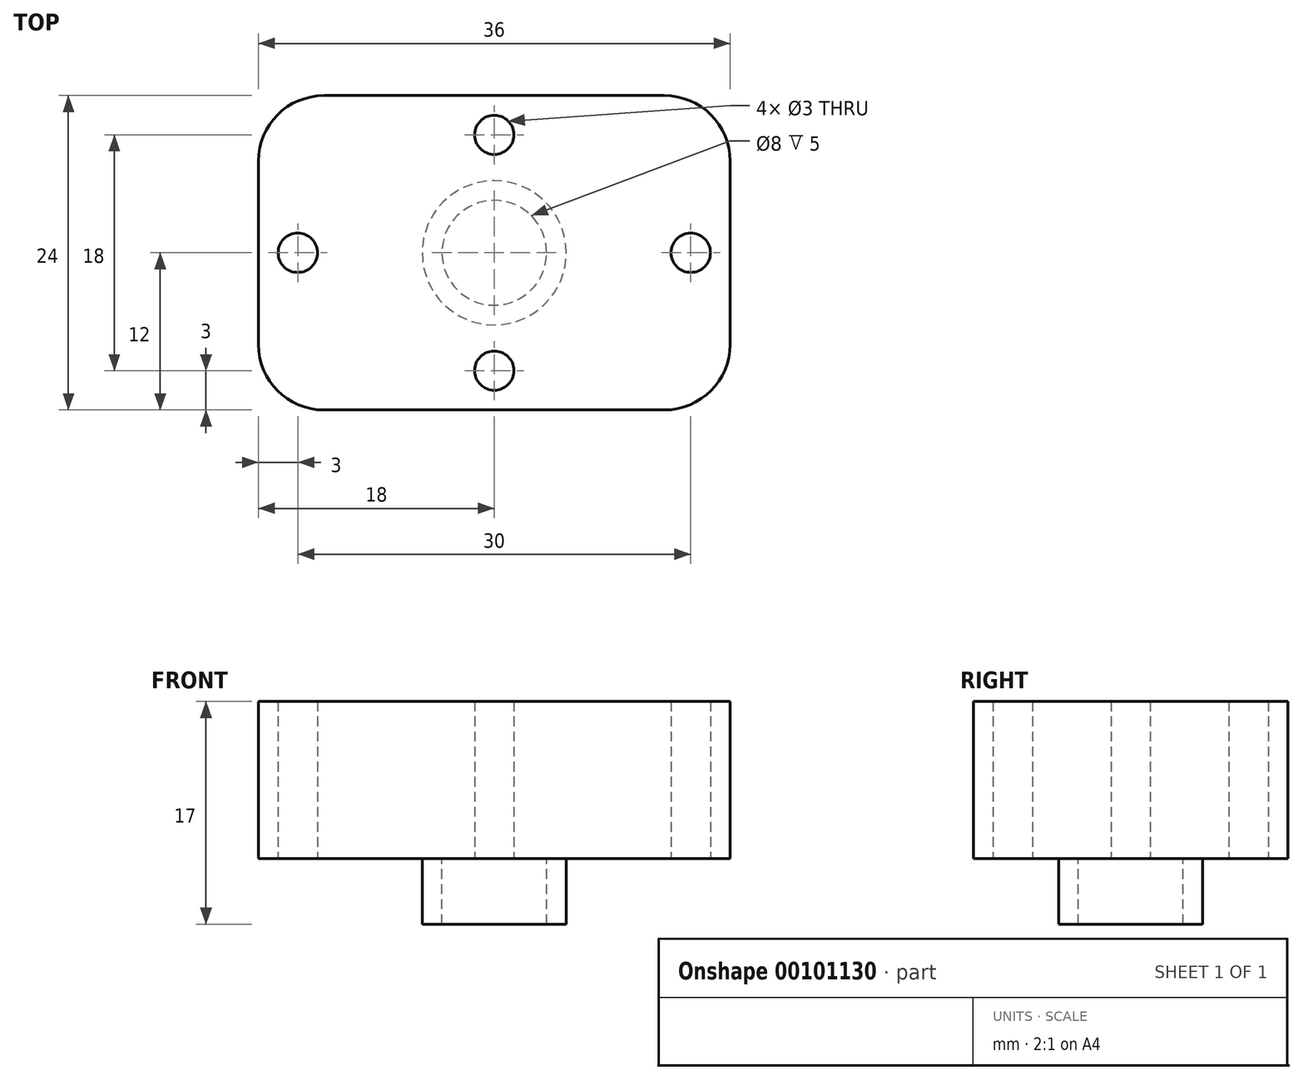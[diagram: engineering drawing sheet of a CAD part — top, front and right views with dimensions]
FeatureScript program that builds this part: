
annotation { "Feature Type Name" : "Feature", "Feature Type Description" : "" }
export const myFeature = defineFeature(function(context is Context, id is Id, definition is map)
    precondition{}
    {
        {
            var Q0;
            Q0=qCreatedBy(makeId("Top.planeOp"),FACE);
            var sketch = newSketch(context, id + "F0", { "sketchPlane" : qUnion([Q0])});
            skLineSegment(sketch, "E0.bottom", {"start": v(-13, 12) * mm, "end": v(13, 12) * mm});
            skLineSegment(sketch, "E0.top", {"start": v(-13, -12) * mm, "end": v(13, -12) * mm});
            skLineSegment(sketch, "E0.left", {"start": v(-18, 7) * mm, "end": v(-18, -7) * mm});
            skLineSegment(sketch, "E0.right", {"start": v(18, 7) * mm, "end": v(18, -7) * mm});
            skPoint(sketch, "E0.middle", {"position": v(0, 0) * mm});
            skPoint(sketch, "E1.visualSharp", {"position": v(-18, 12) * mm});
            skArc(sketch, "E1.filletArc", {"start": v(-13, 12) * mm, "mid": v(-16.54, 10.54) * mm, "end": v(-18, 7) * mm});
            skPoint(sketch, "E2.visualSharp", {"position": v(-18, -12) * mm});
            skArc(sketch, "E2.filletArc", {"start": v(-18, -7) * mm, "mid": v(-16.54, -10.54) * mm, "end": v(-13, -12) * mm});
            skArc(sketch, "E3.filletArc", {"start": v(13, -12) * mm, "mid": v(16.54, -10.54) * mm, "end": v(18, -7) * mm});
            skPoint(sketch, "E4.visualSharp", {"position": v(18, 12) * mm});
            skArc(sketch, "E4.filletArc", {"start": v(18, 7) * mm, "mid": v(16.54, 10.54) * mm, "end": v(13, 12) * mm});
            skPoint(sketch, "E5", {"position": v(-15, 0) * mm});
            skPoint(sketch, "E6", {"position": v(0, 9) * mm});
            skPoint(sketch, "E7", {"position": v(15, 0) * mm});
            skPoint(sketch, "E8", {"position": v(0, -9) * mm});
            skCircle(sketch, "E9", {"center": v(0, 0) * mm, "radius": 4 * mm});
            skCircle(sketch, "E10", {"center": v(0, 0) * mm, "radius": 5.5 * mm});
            skSolve(sketch);
        }
        {
            var Q0;
            Q0=makeQuery(id+"F0.imprint","IMPRINT",FACE,{"disambiguationData":[TD([[makeQuery(id+"F0.imprint","IMPRINT",EDGE,{"derivedFrom":sQuery(id+"F0.wireOp",EDGE,"E0.bottom")}),-1.0]])]});
            var Q1;
            Q1=makeQuery(id+"F0.imprint","IMPRINT",FACE,{"disambiguationData":[TD([[makeQuery(id+"F0.imprint","IMPRINT",EDGE,{"derivedFrom":sQuery(id+"F0.wireOp",EDGE,"E9")}),1.0]])]});
            var Q2;
            Q2=makeQuery(id+"F0.imprint","IMPRINT",FACE,{"disambiguationData":[TD([[makeQuery(id+"F0.imprint","IMPRINT",EDGE,{"derivedFrom":sQuery(id+"F0.wireOp",EDGE,"E9")}),-1.0]])]});
            extrude(context, id + "F1", {"entities" : qUnion([Q0, Q1, Q2]), "depth" : 12 * mm});
        }
        {
            var Q0;
            Q0=sQuery(id+"F0.wireOp",VERTEX,"E7");
            var Q1;
            Q1=sQuery(id+"F0.wireOp",VERTEX,"E8");
            var Q2;
            Q2=sQuery(id+"F0.wireOp",VERTEX,"E6");
            var Q3;
            Q3=sQuery(id+"F0.wireOp",VERTEX,"E5");
            var Q4;
            Q4=makeQuery(id+"F1.opExtrude","SWEPT_BODY",BODY,{"disambiguationData":[OSD([sQuery(id+"F0.wireOp",EDGE,"E0.bottom"),sQuery(id+"F0.wireOp",EDGE,"E0.top"),sQuery(id+"F0.wireOp",EDGE,"E0.left"),sQuery(id+"F0.wireOp",EDGE,"E0.right"),sQuery(id+"F0.wireOp",EDGE,"E1.filletArc"),sQuery(id+"F0.wireOp",EDGE,"E2.filletArc"),sQuery(id+"F0.wireOp",EDGE,"E3.filletArc"),sQuery(id+"F0.wireOp",EDGE,"E4.filletArc")])]});
            hole(context, id + "F2", {"style" : HoleStyle.SIMPLE, "endStyle" : HoleEndStyle.THROUGH, "oppositeDirection" : true, "holeDiameter" : 3 * mm, "locations" : qUnion([Q0, Q1, Q2, Q3]), "scope" : qUnion([Q4]), "isTappedThrough" : true});
        }
        {
            var Q0;
            Q0=makeQuery(id+"F0.imprint","IMPRINT",FACE,{"disambiguationData":[TD([[makeQuery(id+"F0.imprint","IMPRINT",EDGE,{"derivedFrom":sQuery(id+"F0.wireOp",EDGE,"E0.bottom")}),-1.0]])]});
            var sketch = newSketch(context, id + "F3", { "sketchPlane" : qUnion([Q0])});
            skCircle(sketch, "E11", {"center": v(0, -9) * mm, "radius": 1.5 * mm});
            skCircle(sketch, "E12", {"center": v(0, 9) * mm, "radius": 1.5 * mm});
            skCircle(sketch, "E13", {"center": v(0, 9) * mm, "radius": 2.5 * mm});
            skCircle(sketch, "E14", {"center": v(0, -9) * mm, "radius": 2.5 * mm});
            skSolve(sketch);
        }
        {
            var Q0;
            Q0 = qSketchRegion(id + "F3", true);
            extrude(context, id + "F4", {"entities" : qUnion([Q0]), "operationType" : NewBodyOperationType.ADD, "endBound" : BoundingType.UP_TO_NEXT, "depth" : 25 * mm});
        }
        {
            var Q0;
            {var subQ0=sQuery(id+"F3.wireOp",EDGE,"E11");var subQ1=makeQuery(id+"F0.imprint","IMPRINT",EDGE,{"derivedFrom":sQuery(id+"F0.wireOp",EDGE,"E10")});var subQ2=makeQuery(id+"F3.imprint","INTERSECT",VERTEX,{"disambiguationData":[OD(0.0)],"derivedFrom":[subQ1,subQ0]});Q0=makeQuery(id+"F3.imprint","IMPRINT",FACE,{"disambiguationData":[TD([[makeQuery(id+"F3.imprint","IMPRINT",EDGE,{"disambiguationData":[TD([[subQ2,1.0]])],"derivedFrom":subQ0}),-1.0]])]});}
            var Q1;
            {var subQ0=sQuery(id+"F3.wireOp",EDGE,"E12");var subQ1=makeQuery(id+"F0.imprint","IMPRINT",EDGE,{"derivedFrom":sQuery(id+"F0.wireOp",EDGE,"E10")});var subQ2=makeQuery(id+"F3.imprint","INTERSECT",VERTEX,{"disambiguationData":[OD(0.0)],"derivedFrom":[subQ1,subQ0]});Q1=makeQuery(id+"F3.imprint","IMPRINT",FACE,{"disambiguationData":[TD([[makeQuery(id+"F3.imprint","IMPRINT",EDGE,{"disambiguationData":[TD([[subQ2,-1.0]])],"derivedFrom":subQ0}),-1.0]])]});}
            var Q2;
            Q2=makeQuery(id+"F1.opExtrude","SWEPT_BODY",BODY,{"disambiguationData":[OSD([sQuery(id+"F0.wireOp",EDGE,"E0.bottom"),sQuery(id+"F0.wireOp",EDGE,"E0.top"),sQuery(id+"F0.wireOp",EDGE,"E0.left"),sQuery(id+"F0.wireOp",EDGE,"E0.right"),sQuery(id+"F0.wireOp",EDGE,"E1.filletArc"),sQuery(id+"F0.wireOp",EDGE,"E2.filletArc"),sQuery(id+"F0.wireOp",EDGE,"E3.filletArc"),sQuery(id+"F0.wireOp",EDGE,"E4.filletArc"),sQuery(id+"F0.wireOp",EDGE,"E10")])]});
            extrude(context, id + "F5", {"entities" : qUnion([Q0, Q1]), "operationType" : NewBodyOperationType.ADD, "endBoundEntityBody" : qUnion([Q2]), "depth" : 4 * mm});
        }
        {
            var Q0;
            Q0=makeQuery(id+"F0.imprint","IMPRINT",FACE,{"disambiguationData":[TD([[makeQuery(id+"F0.imprint","IMPRINT",EDGE,{"derivedFrom":sQuery(id+"F0.wireOp",EDGE,"E9")}),-1.0]])]});
            extrude(context, id + "F6", {"entities" : qUnion([Q0]), "operationType" : NewBodyOperationType.ADD, "oppositeDirection" : true, "depth" : 5 * mm});
        }
    });
